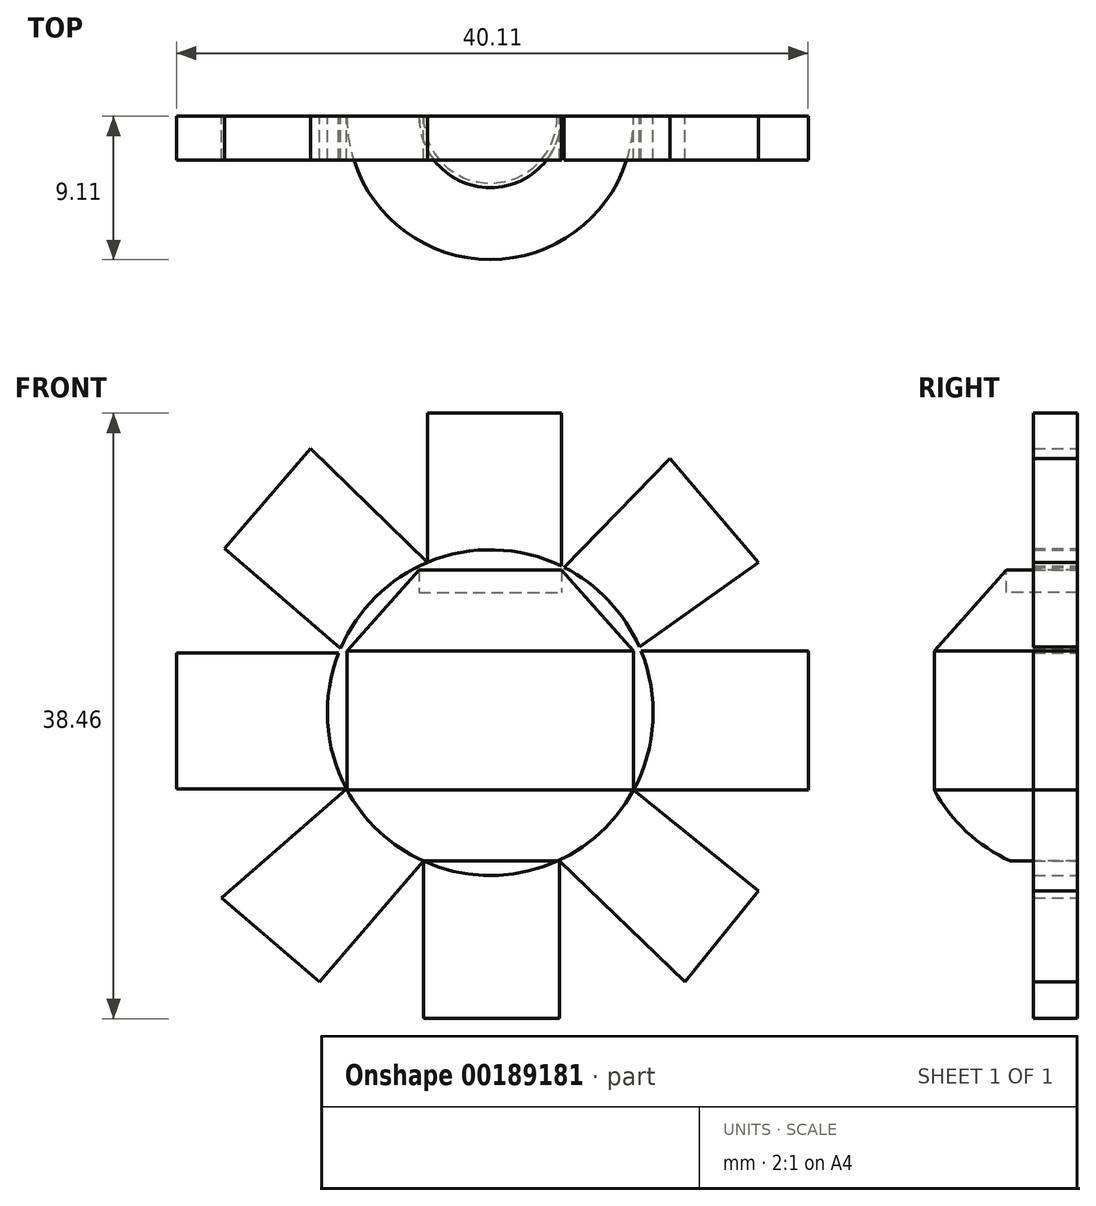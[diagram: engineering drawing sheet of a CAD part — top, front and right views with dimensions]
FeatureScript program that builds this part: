
annotation { "Feature Type Name" : "Feature", "Feature Type Description" : "" }
export const myFeature = defineFeature(function(context is Context, id is Id, definition is map)
    precondition{}
    {
        {
            var Q0;
            Q0=qCreatedBy(makeId("Front.planeOp"),FACE);
            var sketch = newSketch(context, id + "F0", { "sketchPlane" : qUnion([Q0])});
            skCircle(sketch, "E0", {"center": v(0, 0) * mm, "radius": 10.34 * mm});
            skLineSegment(sketch, "E1.bottom", {"start": v(-19.92, 3.78) * mm, "end": v(-9.14, 3.78) * mm});
            skLineSegment(sketch, "E1.top", {"start": v(-19.92, -4.85) * mm, "end": v(-9.14, -4.85) * mm});
            skLineSegment(sketch, "E1.left", {"start": v(-19.92, 3.78) * mm, "end": v(-19.92, -4.85) * mm});
            skLineSegment(sketch, "E1.right", {"start": v(-9.14, 3.78) * mm, "end": v(-9.14, -4.85) * mm});
            skLineSegment(sketch, "E2.bottom", {"start": v(20.2, 3.91) * mm, "end": v(9.1, 3.91) * mm});
            skLineSegment(sketch, "E2.top", {"start": v(20.2, -4.9) * mm, "end": v(9.1, -4.9) * mm});
            skLineSegment(sketch, "E2.left", {"start": v(20.2, 3.91) * mm, "end": v(20.2, -4.9) * mm});
            skLineSegment(sketch, "E2.right", {"start": v(9.1, 3.91) * mm, "end": v(9.1, -4.9) * mm});
            skLineSegment(sketch, "E3.bottom", {"start": v(4.53, 19.02) * mm, "end": v(-3.98, 19.02) * mm});
            skLineSegment(sketch, "E3.top", {"start": v(4.53, 7.62) * mm, "end": v(-3.98, 7.62) * mm});
            skLineSegment(sketch, "E3.left", {"start": v(4.53, 19.02) * mm, "end": v(4.53, 7.62) * mm});
            skLineSegment(sketch, "E3.right", {"start": v(-3.98, 19.02) * mm, "end": v(-3.98, 7.62) * mm});
            skLineSegment(sketch, "E4.bottom", {"start": v(4.4, -19.44) * mm, "end": v(-4.25, -19.44) * mm});
            skLineSegment(sketch, "E4.top", {"start": v(4.4, -9.43) * mm, "end": v(-4.25, -9.43) * mm});
            skLineSegment(sketch, "E4.left", {"start": v(4.4, -19.44) * mm, "end": v(4.4, -9.43) * mm});
            skLineSegment(sketch, "E4.right", {"start": v(-4.25, -19.44) * mm, "end": v(-4.25, -9.43) * mm});
            skLineSegment(sketch, "E5", {"start": v(-10.85, -17.1) * mm, "end": v(-4.25, -9.43) * mm});
            skLineSegment(sketch, "E6", {"start": v(-10.85, -17.1) * mm, "end": v(-17.05, -11.77) * mm});
            skLineSegment(sketch, "E7", {"start": v(-17.05, -11.77) * mm, "end": v(-9.14, -4.85) * mm});
            skLineSegment(sketch, "E8", {"start": v(-9.14, 3.78) * mm, "end": v(-16.88, 10.44) * mm});
            skLineSegment(sketch, "E9", {"start": v(-16.88, 10.44) * mm, "end": v(-11.43, 16.77) * mm});
            skLineSegment(sketch, "E10", {"start": v(-11.43, 16.77) * mm, "end": v(-3.98, 9.55) * mm});
            skLineSegment(sketch, "E11", {"start": v(11.4, 16.14) * mm, "end": v(4.53, 9.06) * mm});
            skLineSegment(sketch, "E12", {"start": v(4.53, 9.06) * mm, "end": v(9.1, 3.91) * mm});
            skLineSegment(sketch, "E13", {"start": v(17.03, 9.55) * mm, "end": v(11.4, 16.14) * mm});
            skLineSegment(sketch, "E14", {"start": v(9.1, 3.91) * mm, "end": v(17.03, 9.55) * mm});
            skLineSegment(sketch, "E15", {"start": v(17.03, -11.33) * mm, "end": v(9.1, -4.9) * mm});
            skLineSegment(sketch, "E16", {"start": v(17.03, -11.33) * mm, "end": v(12.36, -17.1) * mm});
            skLineSegment(sketch, "E17", {"start": v(12.36, -17.1) * mm, "end": v(4.4, -9.43) * mm});
            skLineSegment(sketch, "E18", {"start": v(0, 10.34) * mm, "end": v(0, -10.34) * mm});
            skSolve(sketch);
        }
        {
            var Q0;
            {var subQ4=sQuery(id+"F0.wireOp",EDGE,"E2.right");Q0=makeQuery(id+"F0.imprint","IMPRINT",FACE,{"disambiguationData":[TD([[makeQuery(id+"F0.imprint","IMPRINT",EDGE,{"derivedFrom":subQ4}),-1.0]])]});}
            var Q1;
            Q1=sQuery(id+"F0.wireOp",EDGE,"E18");
            revolve(context, id + "F1", {"entities" : qUnion([Q0]), "axis" : qUnion([Q1]), "revolveType" : RevolveType.ONE_DIRECTION, "angle" : 180 * degree});
        }
        {
            var Q0;
            {var subQ2=sQuery(id+"F0.wireOp",EDGE,"E5");Q0=makeQuery(id+"F0.imprint","IMPRINT",FACE,{"disambiguationData":[TD([[makeQuery(id+"F0.imprint","IMPRINT",EDGE,{"derivedFrom":subQ2}),1.0]])]});}
            var Q1;
            {var subQ0=sQuery(id+"F0.wireOp",EDGE,"E1.top");Q1=makeQuery(id+"F0.imprint","IMPRINT",FACE,{"disambiguationData":[TD([[makeQuery(id+"F0.imprint","IMPRINT",EDGE,{"derivedFrom":subQ0}),1.0]])]});}
            var Q2;
            {var subQ4=sQuery(id+"F0.wireOp",EDGE,"E9");Q2=makeQuery(id+"F0.imprint","IMPRINT",FACE,{"disambiguationData":[TD([[makeQuery(id+"F0.imprint","IMPRINT",EDGE,{"derivedFrom":subQ4}),-1.0]])]});}
            var Q3;
            {var subQ1=sQuery(id+"F0.wireOp",EDGE,"E3.bottom");Q3=makeQuery(id+"F0.imprint","IMPRINT",FACE,{"disambiguationData":[TD([[makeQuery(id+"F0.imprint","IMPRINT",EDGE,{"derivedFrom":subQ1}),1.0]])]});}
            var Q4;
            {var subQ5=sQuery(id+"F0.wireOp",EDGE,"E13");Q4=makeQuery(id+"F0.imprint","IMPRINT",FACE,{"disambiguationData":[TD([[makeQuery(id+"F0.imprint","IMPRINT",EDGE,{"derivedFrom":subQ5}),1.0]])]});}
            var Q5;
            {var subQ0=sQuery(id+"F0.wireOp",EDGE,"E2.top");Q5=makeQuery(id+"F0.imprint","IMPRINT",FACE,{"disambiguationData":[TD([[makeQuery(id+"F0.imprint","IMPRINT",EDGE,{"derivedFrom":subQ0}),-1.0]])]});}
            var Q6;
            {var subQ0=sQuery(id+"F0.wireOp",EDGE,"E15");Q6=makeQuery(id+"F0.imprint","IMPRINT",FACE,{"disambiguationData":[TD([[makeQuery(id+"F0.imprint","IMPRINT",EDGE,{"derivedFrom":subQ0}),1.0]])]});}
            var Q7;
            Q7=makeQuery(id+"F0.imprint","IMPRINT",FACE,{"disambiguationData":[TD([[makeQuery(id+"F0.imprint","IMPRINT",EDGE,{"derivedFrom":sQuery(id+"F0.wireOp",EDGE,"E4.bottom")}),-1.0]])]});
            extrude(context, id + "F2", {"entities" : qUnion([Q0, Q1, Q2, Q3, Q4, Q5, Q6, Q7]), "depth" : 2.8 * mm});
        }
    });
